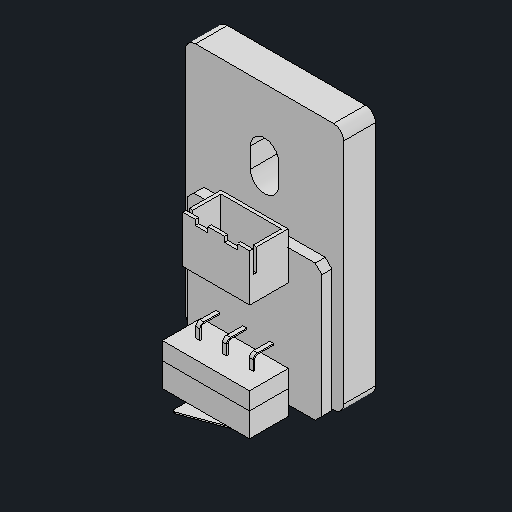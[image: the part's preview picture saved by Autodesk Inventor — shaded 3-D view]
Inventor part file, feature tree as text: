
AUTODESK INVENTOR PART (.ipt)
format: ipt  version: 2024.2 (Build 282272000, 272)  size: 180,224 bytes
history: native  units: mm
features: other x23, extrude x2, chamfer x1
ambient origin geometry x8: Origin, YZ Plane, XZ Plane, XY Plane, X Axis, Y Axis, Z Axis, Center Point
bodies: Body1 (feature_tree), Body2 (feature_tree), Body3 (feature_tree), Body4 (feature_tree), Body5 (feature_tree), Body6 (feature_tree), Body7 (feature_tree), Body8 (feature_tree), Body9 (feature_tree), Body10 (feature_tree), Body11 (feature_tree), Body12 (feature_tree), Body13 (feature_tree)
feature tree (26):
  other  "솔리드1"
  other  "솔리드2"
  other  "솔리드3"
  other  "솔리드4"
  other  "솔리드5"
  other  "솔리드6"
  other  "솔리드7"
  other  "솔리드8"
  other  "솔리드9"
  other  "솔리드10"
  other  "솔리드11"
  other  "솔리드12"
  other  "솔리드13"
  chamfer  "Chamfer1"  [1 undecoded]
  other  "Split1[1]"
  other  "Split1[2]"
  other  "Cut-Extrude3"
  other  "Boss-Extrude5"
  extrude  "Extrude-Thin2"  [1 undecoded]
  other  "LPattern1[1]"
  other  "LPattern1[2]"
  extrude  "Extrude-Thin3"  [1 undecoded]
  other  "LPattern2[1]"
  other  "LPattern2[2]"
  other  "Cut-Extrude4"
  other  "Cut-Extrude5"
note: 3 required parameter values undecoded (feature->parameter linkage not recoverable at this tier; creation-order binding heuristic only, values carry confidence <= 0.55)
